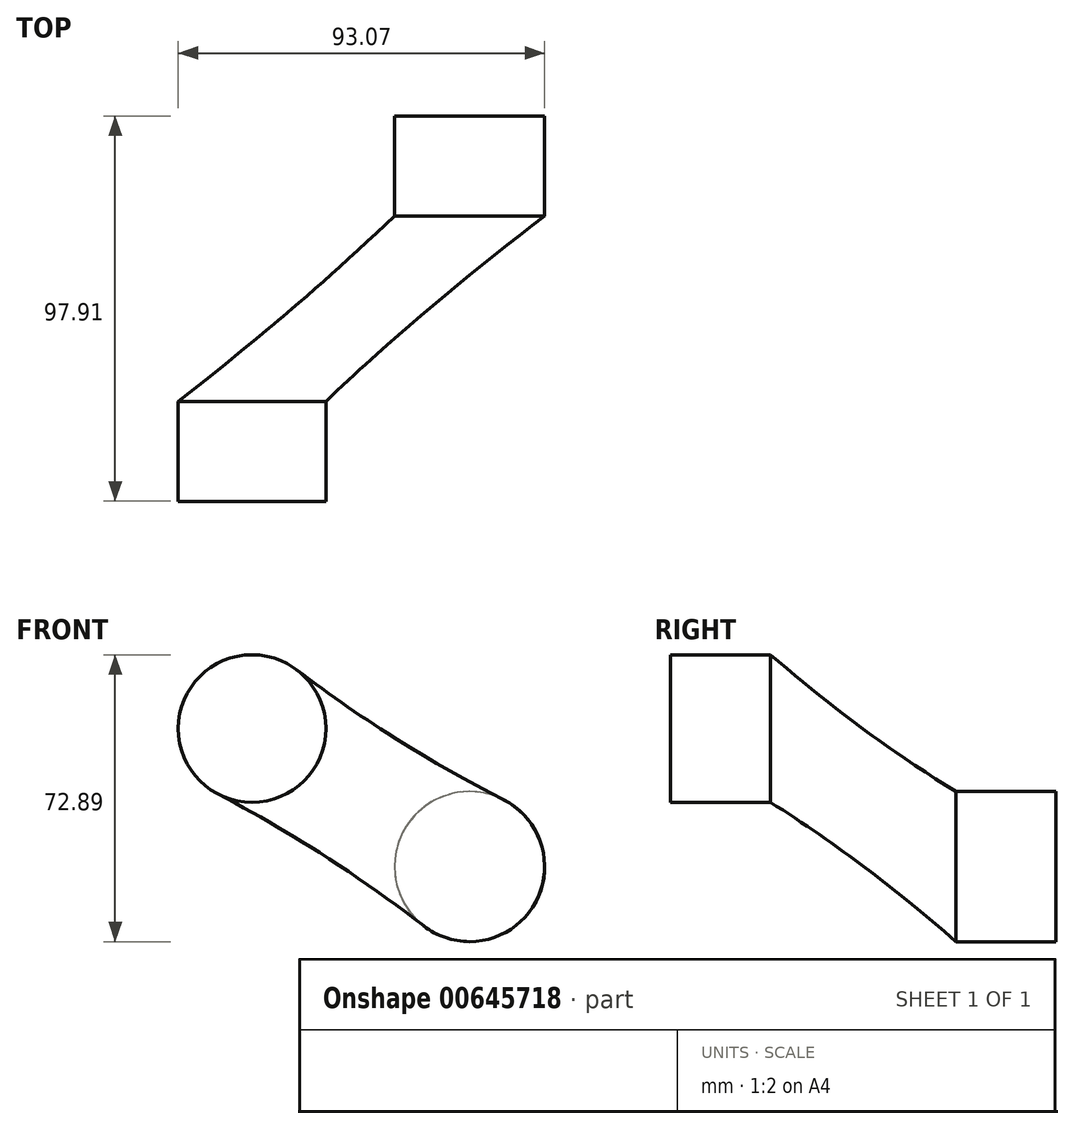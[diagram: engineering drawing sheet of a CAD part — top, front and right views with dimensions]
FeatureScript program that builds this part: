
annotation { "Feature Type Name" : "Feature", "Feature Type Description" : "" }
export const myFeature = defineFeature(function(context is Context, id is Id, definition is map)
    precondition{}
    {
        {
            var Q0;
            Q0=qCreatedBy(makeId("Front.planeOp"),FACE);
            var sketch = newSketch(context, id + "F0", { "sketchPlane" : qUnion([Q0])});
            skCircle(sketch, "E0", {"center": v(0, 0) * mm, "radius": 19.06 * mm});
            skSolve(sketch);
        }
        {
            var Q0;
            Q0=makeQuery(id+"F0.imprint","IMPRINT",FACE,{"disambiguationData":[TD([[makeQuery(id+"F0.imprint","IMPRINT",EDGE,{"derivedFrom":sQuery(id+"F0.wireOp",EDGE,"E0")}),1.0]])]});
            extrude(context, id + "F1", {"entities" : qUnion([Q0]), "depth" : 25.4 * mm, "offsetDistance" : 25.4 * mm});
        }
        {
            var Q0;
            Q0=qCreatedBy(makeId("Front.planeOp"),FACE);
            var sketch = newSketch(context, id + "F2", { "sketchPlane" : qUnion([Q0])});
            skCircle(sketch, "E1", {"center": v(-55.27, 35.09) * mm, "radius": 18.74 * mm});
            skSolve(sketch);
        }
        {
            var Q0;
            Q0=makeQuery(id+"F2.imprint","IMPRINT",FACE,{"disambiguationData":[TD([[makeQuery(id+"F2.imprint","IMPRINT",EDGE,{"derivedFrom":sQuery(id+"F2.wireOp",EDGE,"E1")}),1.0]])]});
            extrude(context, id + "F3", {"entities" : qUnion([Q0]), "depth" : 25.4 * mm, "offsetDistance" : 25.4 * mm});
        }
        {
            var Q0;
            Q0=qCreatedBy(makeId("Top.planeOp"),FACE);
            var sketch = newSketch(context, id + "F4", { "sketchPlane" : qUnion([Q0])});
            skLineSegment(sketch, "E2", {"start": v(-31.33, 43.8) * mm, "end": v(-31.33, -79.5) * mm});
            skSolve(sketch);
        }
        {
            var Q0;
            Q0=makeQuery(id+"F3.opExtrude","SWEPT_BODY",BODY,{"disambiguationData":[OSD([sQuery(id+"F2.wireOp",EDGE,"E1"),sQuery(id+"F2.wireOp",EDGE,"Hr9jmjCi-Y6db-eycK-EI7Z-HuKcVqPmNN5z")])]});
            var Q1;
            Q1=sQuery(id+"F4.wireOp",EDGE,"E2");
            transform(context, id + "F5", {"entities" : qUnion([Q0]), "transformType" : TransformType.TRANSLATION_ENTITY, "oppositeDirectionEntity" : false, "transformLine" : qUnion([Q1]), "makeCopy" : false});
        }
        {
            var Q0;
            Q0=qCreatedBy(makeId("Right.planeOp"),FACE);
            var sketch = newSketch(context, id + "F6", { "sketchPlane" : qUnion([Q0])});
            skLineSegment(sketch, "E3", {"start": v(0, 27.18) * mm, "end": v(-32.7, 27.18) * mm});
            skSolve(sketch);
        }
        {
            var Q0;
            Q0=makeQuery(id+"F1.opExtrude","SWEPT_BODY",BODY,{"disambiguationData":[OSD([sQuery(id+"F0.wireOp",EDGE,"E0"),sQuery(id+"F0.wireOp",EDGE,"9xzUHAmL-oGrC-UhRV-vkyZ-Xbi0LoqIhojR")])]});
            var Q1;
            Q1=sQuery(id+"F6.wireOp",EDGE,"E3");
            transform(context, id + "F7", {"entities" : qUnion([Q0]), "transformType" : TransformType.TRANSLATION_DISTANCE, "transformDirection" : qUnion([Q1]), "distance" : 50.8 * mm, "makeCopy" : false});
        }
        {
            var Q0;
            Q0=makeQuery(id+"F1.opExtrude","CAP_FACE",FACE,{"disambiguationData":[OSD([sQuery(id+"F0.wireOp",EDGE,"E0")])],"isStart":false});
            var Q1;
            Q1=makeQuery(id+"F3.opExtrude","CAP_FACE",FACE,{"disambiguationData":[OSD([sQuery(id+"F2.wireOp",EDGE,"E1")])],"isStart":true});
            loft(context, id + "F8", {"sheetProfilesArray" : [{ "sheetProfileEntities" : qUnion([Q0]) }, { "sheetProfileEntities" : qUnion([Q1]) }]});
        }
    });
